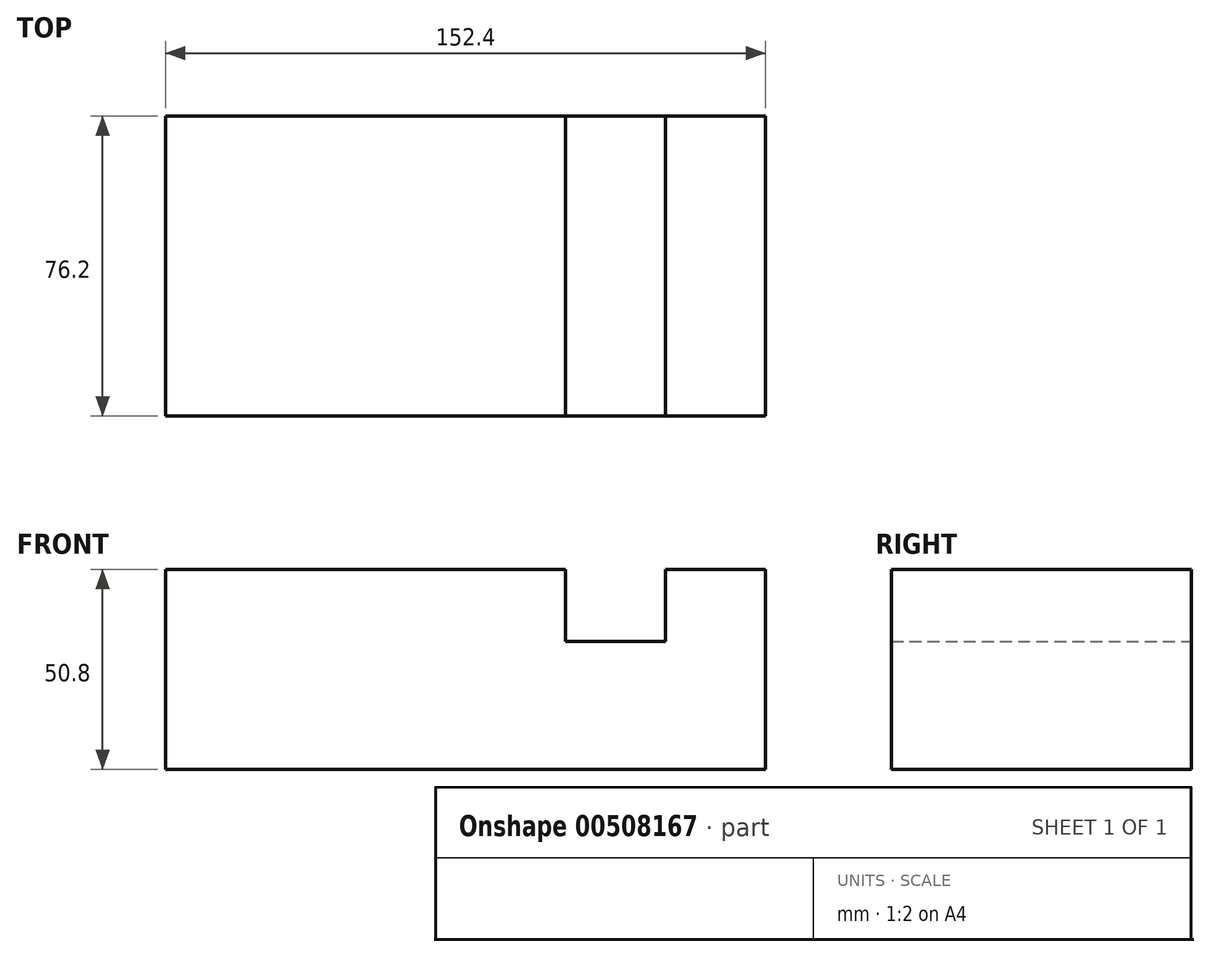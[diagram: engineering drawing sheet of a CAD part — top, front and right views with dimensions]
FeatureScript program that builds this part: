
annotation { "Feature Type Name" : "Feature", "Feature Type Description" : "" }
export const myFeature = defineFeature(function(context is Context, id is Id, definition is map)
    precondition{}
    {
        {
            var Q0;
            Q0=qCreatedBy(makeId("Front.planeOp"),FACE);
            var sketch = newSketch(context, id + "F0", { "sketchPlane" : qUnion([Q0])});
            skLineSegment(sketch, "E0", {"start": v(63.45, 32.87) * mm, "end": v(38.05, 32.87) * mm});
            skLineSegment(sketch, "E1", {"start": v(38.05, 32.87) * mm, "end": v(38.05, 14.57) * mm});
            skLineSegment(sketch, "E2", {"start": v(38.05, 14.57) * mm, "end": v(12.65, 14.57) * mm});
            skLineSegment(sketch, "E3", {"start": v(12.65, 14.57) * mm, "end": v(12.65, 32.87) * mm});
            skLineSegment(sketch, "E4", {"start": v(12.65, 32.87) * mm, "end": v(-88.95, 32.87) * mm});
            skLineSegment(sketch, "E5", {"start": v(-88.95, 32.87) * mm, "end": v(-88.95, -17.93) * mm});
            skLineSegment(sketch, "E6", {"start": v(-88.95, -17.93) * mm, "end": v(63.45, -17.93) * mm});
            skLineSegment(sketch, "E7", {"start": v(63.45, -17.93) * mm, "end": v(63.45, 32.87) * mm});
            skSolve(sketch);
        }
        {
            var Q0;
            Q0=makeQuery(id+"F0.imprint","IMPRINT",FACE,{"disambiguationData":[TD([[makeQuery(id+"F0.imprint","IMPRINT",EDGE,{"derivedFrom":sQuery(id+"F0.wireOp",EDGE,"E0")}),1.0]])]});
            extrude(context, id + "F1", {"entities" : qUnion([Q0]), "depth" : 76.2 * mm});
        }
    });
